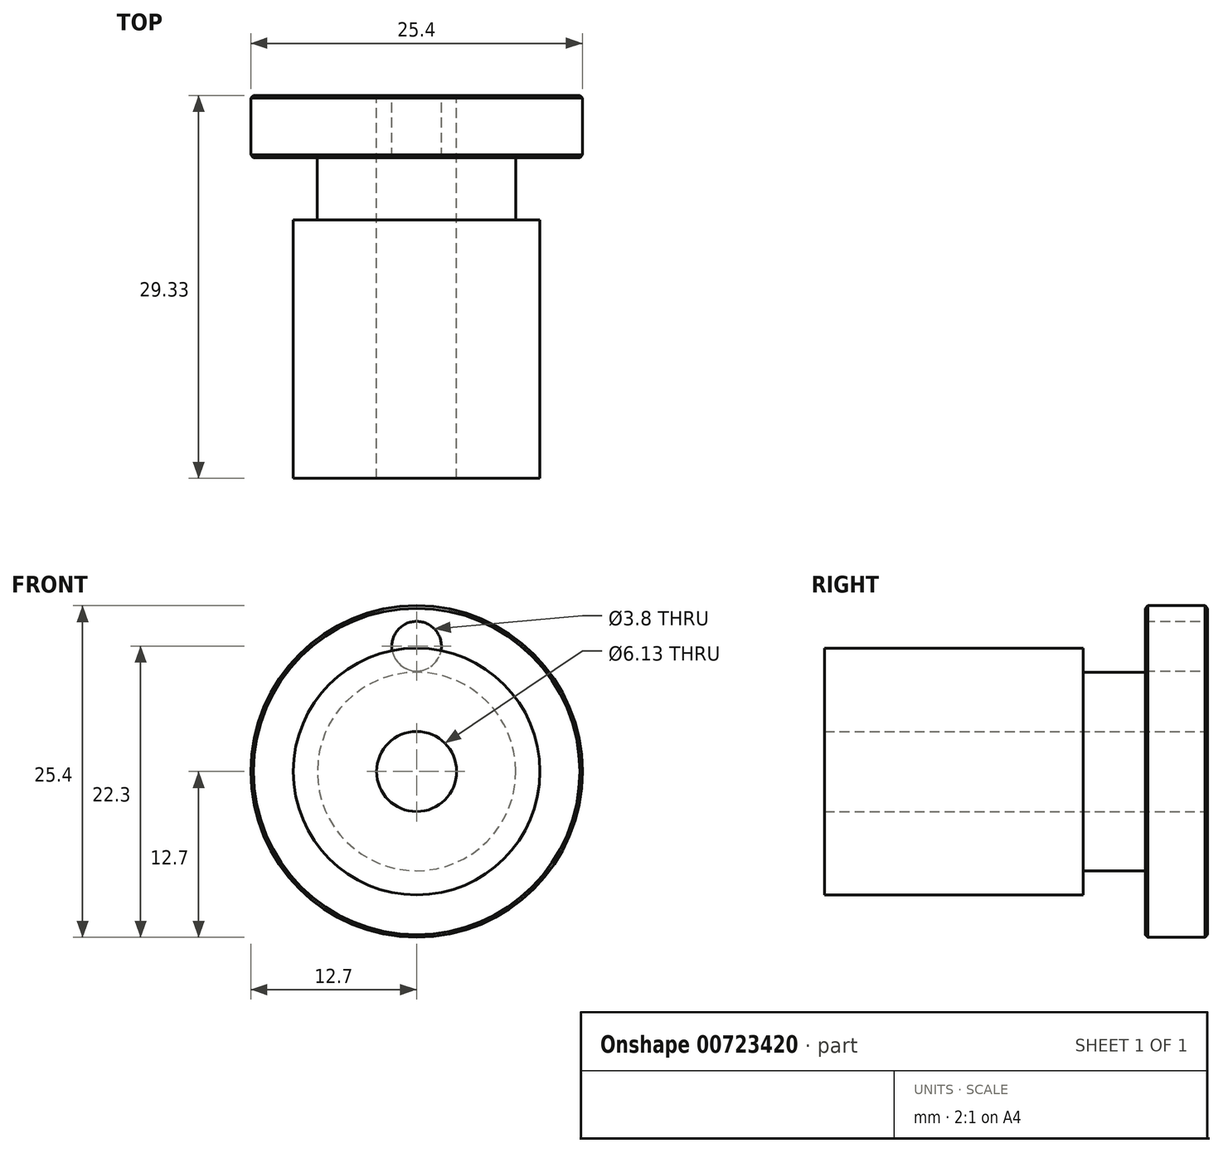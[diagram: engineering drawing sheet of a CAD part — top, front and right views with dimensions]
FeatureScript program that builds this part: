
annotation { "Feature Type Name" : "Feature", "Feature Type Description" : "" }
export const myFeature = defineFeature(function(context is Context, id is Id, definition is map)
    precondition{}
    {
        {
            var Q0;
            Q0=qCreatedBy(makeId("Front.planeOp"),FACE);
            var sketch = newSketch(context, id + "F0", { "sketchPlane" : qUnion([Q0])});
            skCircle(sketch, "E0", {"center": v(0, 0) * mm, "radius": 12.7 * mm});
            skSolve(sketch);
        }
        {
            var Q0;
            Q0=makeQuery(id+"F0.imprint","IMPRINT",FACE,{"disambiguationData":[TD([[makeQuery(id+"F0.imprint","IMPRINT",EDGE,{"derivedFrom":sQuery(id+"F0.wireOp",EDGE,"E0")}),1.0]])]});
            extrude(context, id + "F1", {"entities" : qUnion([Q0]), "depth" : 4.76 * mm, "offsetDistance" : 25 * mm});
        }
        {
            var Q0;
            Q0=makeQuery(id+"F1.opExtrude","CAP_FACE",FACE,{"disambiguationData":[OSD([sQuery(id+"F0.wireOp",EDGE,"E0")])],"isStart":false});
            var sketch = newSketch(context, id + "F2", { "sketchPlane" : qUnion([Q0])});
            skCircle(sketch, "E1", {"center": v(0, 0) * mm, "radius": 7.6 * mm});
            skSolve(sketch);
        }
        {
            var Q0;
            Q0=makeQuery(id+"F2.imprint","IMPRINT",FACE,{"disambiguationData":[TD([[makeQuery(id+"F2.imprint","IMPRINT",EDGE,{"derivedFrom":sQuery(id+"F2.wireOp",EDGE,"E1")}),1.0]])]});
            extrude(context, id + "F3", {"entities" : qUnion([Q0]), "operationType" : NewBodyOperationType.ADD, "depth" : 4.76 * mm, "offsetDistance" : 25 * mm});
        }
        {
            var Q0;
            Q0=makeQuery(id+"F3.opExtrude","CAP_FACE",FACE,{"disambiguationData":[OSD([sQuery(id+"F2.wireOp",EDGE,"E1")])],"isStart":false});
            var sketch = newSketch(context, id + "F4", { "sketchPlane" : qUnion([Q0])});
            skCircle(sketch, "E2", {"center": v(0, 0) * mm, "radius": 9.45 * mm});
            skSolve(sketch);
        }
        {
            var Q0;
            Q0=makeQuery(id+"F4.imprint","IMPRINT",FACE,{"disambiguationData":[TD([[makeQuery(id+"F4.imprint","IMPRINT",EDGE,{"derivedFrom":sQuery(id+"F4.wireOp",EDGE,"E2")}),1.0]])]});
            var Q1;
            Q1=makeQuery(id+"F4.imprint","IMPRINT",FACE,{"disambiguationData":[TD([[makeQuery(id+"F4.imprint","IMPRINT",EDGE,{"derivedFrom":makeQuery(id+"F3.opExtrude","CAP_EDGE",EDGE,{"disambiguationData":[OSD([sQuery(id+"F2.wireOp",EDGE,"E1")])],"isStart":false})}),1.0]])]});
            extrude(context, id + "F5", {"entities" : qUnion([Q0, Q1]), "operationType" : NewBodyOperationType.ADD, "depth" : 19.8 * mm, "offsetDistance" : 25 * mm});
        }
        {
            var Q0;
            Q0=makeQuery(id+"F1.opExtrude","CAP_EDGE",EDGE,{"disambiguationData":[OSD([sQuery(id+"F0.wireOp",EDGE,"E0")])],"isStart":true});
            var Q1;
            Q1=makeQuery(id+"F1.opExtrude","CAP_EDGE",EDGE,{"disambiguationData":[OSD([sQuery(id+"F0.wireOp",EDGE,"E0")])],"isStart":false});
            chamfer(context, id + "F6", {"entities" : qUnion([Q0, Q1]), "width" : 0.2 * mm, "tangentPropagation" : true});
        }
        {
            var Q0;
            Q0=makeQuery(id+"F1.opExtrude","CAP_FACE",FACE,{"disambiguationData":[OSD([sQuery(id+"F0.wireOp",EDGE,"E0")])],"isStart":true});
            var sketch = newSketch(context, id + "F7", { "sketchPlane" : qUnion([Q0])});
            skCircle(sketch, "E3", {"center": v(0, 9.6) * mm, "radius": 1.9 * mm});
            skSolve(sketch);
        }
        {
            var Q0;
            Q0=qCreatedBy(makeId("Right.planeOp"),FACE);
            var sketch = newSketch(context, id + "F8", { "sketchPlane" : qUnion([Q0])});
            skLineSegment(sketch, "E4", {"start": v(5.38, 0) * mm, "end": v(-53.55, 0) * mm, "construction": true});
            skSolve(sketch);
        }
        {
            var Q0;
            Q0 = qSketchRegion(id + "F7", true);
            var Q1;
            Q1=makeQuery(id+"F1.opExtrude","CAP_FACE",FACE,{"disambiguationData":[OSD([sQuery(id+"F0.wireOp",EDGE,"E0")])],"isStart":false});
            extrude(context, id + "F9", {"entities" : qUnion([Q0]), "operationType" : NewBodyOperationType.REMOVE, "endBound" : BoundingType.UP_TO_SURFACE, "oppositeDirection" : true, "depth" : 25 * mm, "endBoundEntityFace" : qUnion([Q1]), "offsetDistance" : 25 * mm});
        }
        {
            var Q0;
            Q0=makeQuery(id+"F1.opExtrude","CAP_FACE",FACE,{"disambiguationData":[OSD([sQuery(id+"F0.wireOp",EDGE,"E0")])],"isStart":true});
            var sketch = newSketch(context, id + "F10", { "sketchPlane" : qUnion([Q0])});
            skCircle(sketch, "E5", {"center": v(0, 0) * mm, "radius": 3.07 * mm});
            skSolve(sketch);
        }
        {
            var Q0;
            Q0 = qSketchRegion(id + "F10", true);
            var Q1;
            Q1=makeQuery(id+"F5.opExtrude","CAP_FACE",FACE,{"disambiguationData":[OSD([sQuery(id+"F4.wireOp",EDGE,"E2")])],"isStart":false});
            extrude(context, id + "F11", {"entities" : qUnion([Q0]), "operationType" : NewBodyOperationType.REMOVE, "endBound" : BoundingType.UP_TO_SURFACE, "oppositeDirection" : true, "depth" : 25 * mm, "endBoundEntityFace" : qUnion([Q1]), "offsetDistance" : 25 * mm});
        }
    });
